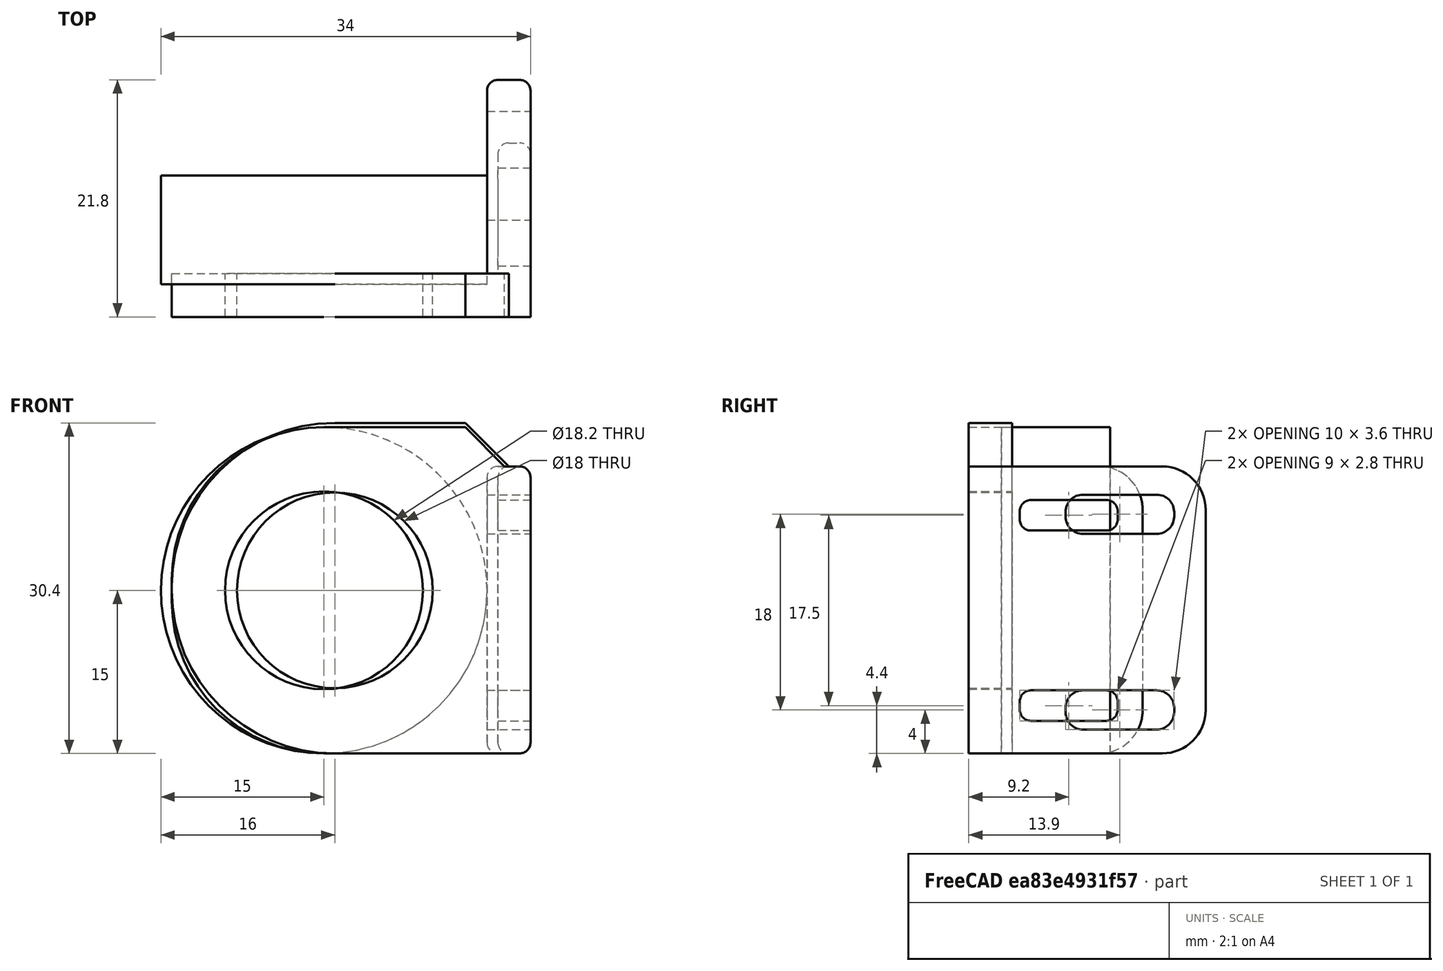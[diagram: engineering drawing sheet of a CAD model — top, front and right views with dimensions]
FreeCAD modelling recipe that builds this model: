
FCSTD DOCUMENT  (FreeCAD 0.18R)
Label: M18 mount
License: All rights reserved
LicenseURL: http://en.wikipedia.org/wiki/All_rights_reserved
objects: Part::Fillet×6, Part::Box×4, Part::Cut×3, Part::Cylinder×2, Mesh::Feature×1, Part::Feature×1, Part::Chamfer×1, Part::MultiFuse×1
note: 18 computed .brp shape members not serialized (recipe doc carries the construction recipe); baked Part::Feature solids carry a one-line shape summary decoded from their .brp

FEATURE [Mesh::Feature] EZABLTouch_Plate_V1
  Placement = pos=(631.5,153.6,71.79) rot=(0.57735,0.57735,-0.57735;4.18879rad)
FEATURE [Part::Feature] Part__Feature  label="M18"
  shape: bbox 33 x 16.33 x 30.73 mm, 45 faces (baked)
FEATURE [Part::Box] Box  label="Cubo"
  AttacherType = Attacher::AttachEngine3D
  Height = 30
  Length = 33
  Placement = pos=(597,176,57) rot=(0,0,1;0rad)
  Width = 4
FEATURE [Part::Box] Box001  label="Cubo001"
  AttacherType = Attacher::AttachEngine3D
  Height = 26.4
  Length = 4
  Placement = pos=(626,176,57) rot=(0,0,1;0rad)
  Width = 21.8
FEATURE [Part::Fillet] Fillet
  Base = -> Box
  Edges = 2 edges r=14: [Edge2,Edge4]
FEATURE [Part::Fillet] Fillet001
  Base = -> Box001
  Edges = 2 edges r=4: [Edge11,Edge12]
FEATURE [Part::Fillet] Fillet002
  Base = -> Fillet001
  Edges = 6 edges r=1: [Edge1,Edge4,Edge5,Edge9,Edge14,Edge17]
FEATURE [Part::Box] Box002  label="Cubo002"
  AttacherType = Attacher::AttachEngine3D
  Height = 3.6
  Length = 10
  Placement = pos=(621,184.9,59.2) rot=(0,0,1;0rad)
  Width = 10
FEATURE [Part::Fillet] Fillet003
  Base = -> Box002
  Edges = 4 edges r=1.6: [Edge9,Edge10,Edge11,Edge12]
FEATURE [Part::Box] Box003  label="Cubo003"
  AttacherType = Attacher::AttachEngine3D
  Height = 3.6
  Length = 10
  Placement = pos=(621,184.9,59.2) rot=(0,0,1;0rad)
  Width = 10
FEATURE [Part::Fillet] Fillet004
  Base = -> Box003
  Edges = 4 edges r=1.6: [Edge9,Edge10,Edge11,Edge12]
  Placement = pos=(0,0,18) rot=(0,0,1;0rad)
FEATURE [Part::Cut] Cut
  Base = -> Fillet002
  Tool = -> Fillet003
FEATURE [Part::Cut] Cut001
  Base = -> Cut
  Tool = -> Fillet004
FEATURE [Part::Fillet] Fillet005
  Base = -> Fillet
  Edges = 1 edges r=1: [Edge17]
FEATURE [Part::Chamfer] Chamfer
  Base = -> Fillet005
  Edges = 1 edges r=6: [Edge15]
FEATURE [Part::MultiFuse] Fusion
  Shapes = -> [Cut001,Chamfer]
FEATURE [Part::Cylinder] Cylinder  label="Cilindro"
  Angle = 360
  AttacherType = Attacher::AttachEngine3D
  Height = 10
  Placement = pos=(611,179,72) rot=(1,0,0;4.71239rad)
  Radius = 15
FEATURE [Part::Cylinder] Cylinder001  label="Cilindro001"
  Angle = 360
  AttacherType = Attacher::AttachEngine3D
  Height = 20
  Placement = pos=(611,168,72) rot=(-1,0,0;1.5708rad)
  Radius = 9.1
FEATURE [Part::Cut] Cut002
  Base = -> Fusion
  Tool = -> Cylinder001
